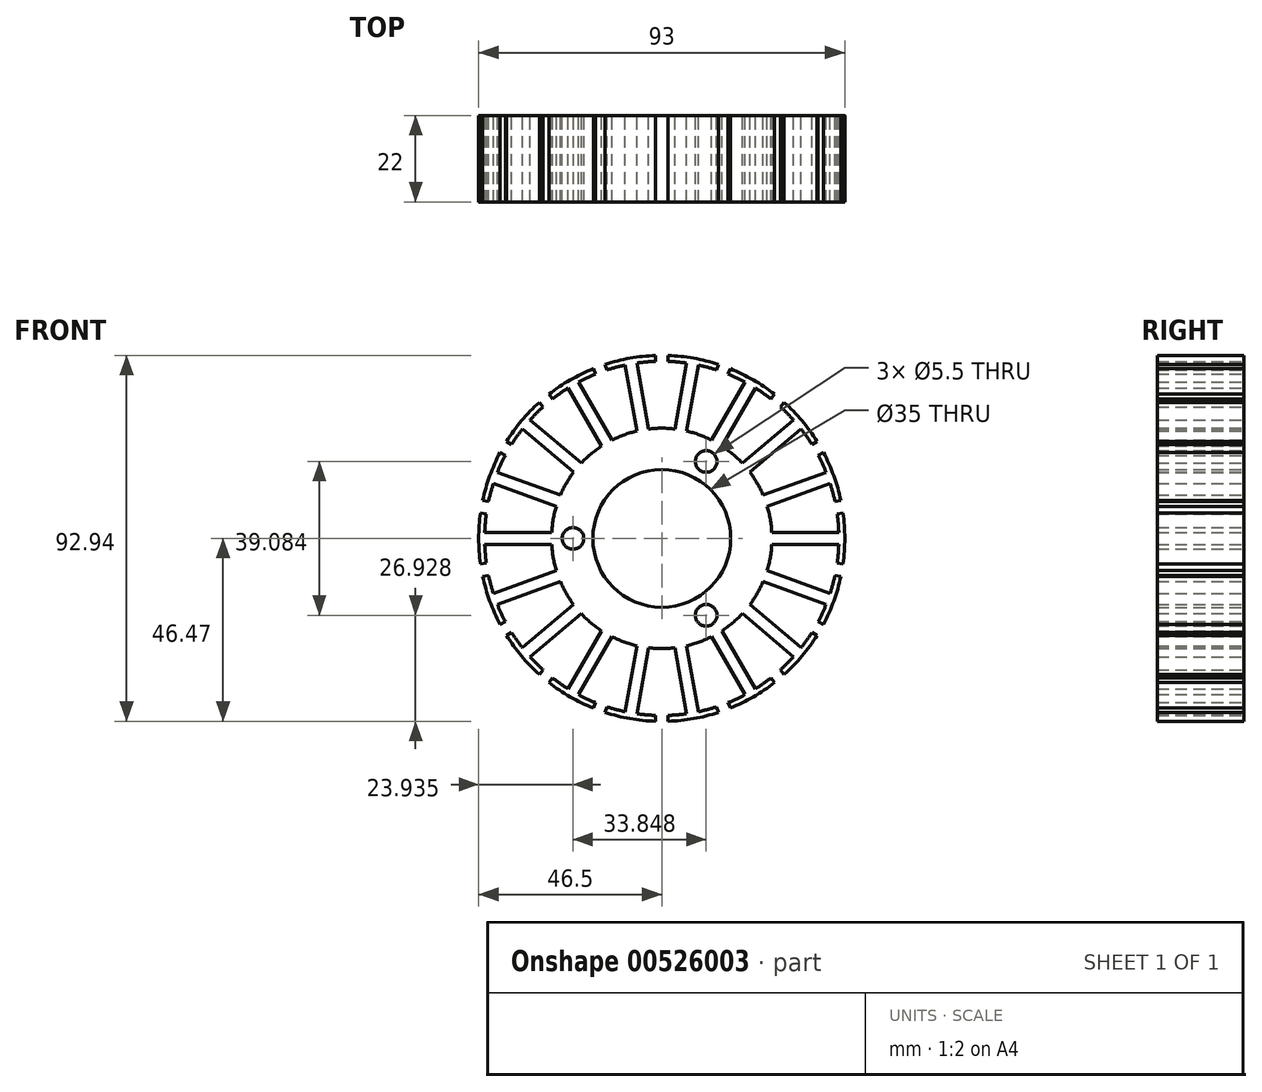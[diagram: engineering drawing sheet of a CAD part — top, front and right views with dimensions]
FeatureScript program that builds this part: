
annotation { "Feature Type Name" : "Feature", "Feature Type Description" : "" }
export const myFeature = defineFeature(function(context is Context, id is Id, definition is map)
    precondition{}
    {
        {
            var Q0;
            Q0=qCreatedBy(makeId("Front.planeOp"),FACE);
            var sketch = newSketch(context, id + "F0", { "sketchPlane" : qUnion([Q0])});
            skCircle(sketch, "E0", {"center": v(0, 0) * mm, "radius": 17.5 * mm});
            skArc(sketch, "E1", {"start": v(-46.04, 6.5) * mm, "mid": v(-46.5, 0) * mm, "end": v(-46.04, -6.5) * mm});
            skArc(sketch, "E2", {"start": v(-27.96, -1.5) * mm, "mid": v(-27.57, -4.86) * mm, "end": v(-26.79, -8.15) * mm});
            skLineSegment(sketch, "E3", {"start": v(-27.96, 1.5) * mm, "end": v(-44.97, 1.5) * mm});
            skLineSegment(sketch, "E4", {"start": v(-27.96, -1.5) * mm, "end": v(-44.97, -1.5) * mm});
            skArc(sketch, "E5", {"start": v(-44.56, 6.25) * mm, "mid": v(-44.83, 3.88) * mm, "end": v(-44.97, 1.5) * mm});
            skLineSegment(sketch, "E6", {"start": v(-46.04, 6.5) * mm, "end": v(-44.56, 6.25) * mm});
            skLineSegment(sketch, "E7", {"start": v(-46.04, -6.5) * mm, "end": v(-44.56, -6.25) * mm});
            skArc(sketch, "E8.trimOffspring", {"start": v(-44.97, -1.5) * mm, "mid": v(-44.83, -3.88) * mm, "end": v(-44.56, -6.25) * mm});
            skLineSegment(sketch, "E9.1.0", {"start": v(-26.79, 8.15) * mm, "end": v(-42.78, 13.97) * mm});
            skArc(sketch, "E9.1.1", {"start": v(-39.74, 21.11) * mm, "mid": v(-40.8, 18.98) * mm, "end": v(-41.75, 16.8) * mm});
            skArc(sketch, "E9.1.2", {"start": v(-42.78, 13.97) * mm, "mid": v(-43.46, 11.69) * mm, "end": v(-44.01, 9.37) * mm});
            skLineSegment(sketch, "E9.1.3", {"start": v(-25.76, 10.97) * mm, "end": v(-41.75, 16.8) * mm});
            skArc(sketch, "E9.1.4", {"start": v(-41.04, 21.86) * mm, "mid": v(-43.7, 15.9) * mm, "end": v(-45.49, 9.64) * mm});
            skLineSegment(sketch, "E9.1.5", {"start": v(-41.04, 21.86) * mm, "end": v(-39.74, 21.11) * mm});
            skLineSegment(sketch, "E9.1.6", {"start": v(-45.49, 9.64) * mm, "end": v(-44.01, 9.37) * mm});
            skLineSegment(sketch, "E9.2.0", {"start": v(-22.38, 16.82) * mm, "end": v(-35.42, 27.76) * mm});
            skArc(sketch, "E9.2.1", {"start": v(-30.12, 33.43) * mm, "mid": v(-31.85, 31.8) * mm, "end": v(-33.49, 30.06) * mm});
            skArc(sketch, "E9.2.2", {"start": v(-35.42, 27.76) * mm, "mid": v(-36.84, 25.85) * mm, "end": v(-38.16, 23.86) * mm});
            skLineSegment(sketch, "E9.2.3", {"start": v(-20.45, 19.12) * mm, "end": v(-33.49, 30.06) * mm});
            skArc(sketch, "E9.2.4", {"start": v(-31.1, 34.58) * mm, "mid": v(-35.62, 29.89) * mm, "end": v(-39.45, 24.62) * mm});
            skLineSegment(sketch, "E9.2.5", {"start": v(-31.1, 34.58) * mm, "end": v(-30.12, 33.43) * mm});
            skLineSegment(sketch, "E9.2.6", {"start": v(-39.45, 24.62) * mm, "end": v(-38.16, 23.86) * mm});
            skLineSegment(sketch, "E9.3.0", {"start": v(-15.28, 23.46) * mm, "end": v(-23.79, 38.2) * mm});
            skArc(sketch, "E9.3.1", {"start": v(-16.87, 41.72) * mm, "mid": v(-19.06, 40.77) * mm, "end": v(-21.19, 39.7) * mm});
            skArc(sketch, "E9.3.2", {"start": v(-23.79, 38.2) * mm, "mid": v(-25.78, 36.89) * mm, "end": v(-27.7, 35.47) * mm});
            skLineSegment(sketch, "E9.3.3", {"start": v(-12.68, 24.96) * mm, "end": v(-21.19, 39.7) * mm});
            skArc(sketch, "E9.3.4", {"start": v(-17.4, 43.12) * mm, "mid": v(-23.25, 40.27) * mm, "end": v(-28.65, 36.62) * mm});
            skLineSegment(sketch, "E9.3.5", {"start": v(-17.4, 43.12) * mm, "end": v(-16.87, 41.72) * mm});
            skLineSegment(sketch, "E9.3.6", {"start": v(-28.65, 36.62) * mm, "end": v(-27.7, 35.47) * mm});
            skLineSegment(sketch, "E9.4.0", {"start": v(-6.33, 27.27) * mm, "end": v(-9.29, 44.03) * mm});
            skArc(sketch, "E9.4.1", {"start": v(-1.58, 44.97) * mm, "mid": v(-3.96, 44.83) * mm, "end": v(-6.33, 44.55) * mm});
            skArc(sketch, "E9.4.2", {"start": v(-9.29, 44.03) * mm, "mid": v(-11.6, 43.48) * mm, "end": v(-13.9, 42.8) * mm});
            skLineSegment(sketch, "E9.4.3", {"start": v(-3.38, 27.8) * mm, "end": v(-6.33, 44.55) * mm});
            skArc(sketch, "E9.4.4", {"start": v(-1.6, 46.47) * mm, "mid": v(-8.07, 45.8) * mm, "end": v(-14.4, 44.22) * mm});
            skLineSegment(sketch, "E9.4.5", {"start": v(-1.6, 46.47) * mm, "end": v(-1.58, 44.97) * mm});
            skLineSegment(sketch, "E9.4.6", {"start": v(-14.4, 44.22) * mm, "end": v(-13.9, 42.8) * mm});
            skLineSegment(sketch, "E9.5.0", {"start": v(3.38, 27.8) * mm, "end": v(6.33, 44.55) * mm});
            skArc(sketch, "E9.5.1", {"start": v(13.9, 42.8) * mm, "mid": v(11.6, 43.48) * mm, "end": v(9.29, 44.03) * mm});
            skArc(sketch, "E9.5.2", {"start": v(6.33, 44.55) * mm, "mid": v(3.96, 44.83) * mm, "end": v(1.58, 44.97) * mm});
            skLineSegment(sketch, "E9.5.3", {"start": v(6.33, 27.27) * mm, "end": v(9.29, 44.03) * mm});
            skArc(sketch, "E9.5.4", {"start": v(14.4, 44.22) * mm, "mid": v(8.07, 45.8) * mm, "end": v(1.6, 46.47) * mm});
            skLineSegment(sketch, "E9.5.5", {"start": v(14.4, 44.22) * mm, "end": v(13.9, 42.8) * mm});
            skLineSegment(sketch, "E9.5.6", {"start": v(1.6, 46.47) * mm, "end": v(1.58, 44.97) * mm});
            skLineSegment(sketch, "E9.6.0", {"start": v(12.68, 24.96) * mm, "end": v(21.19, 39.7) * mm});
            skArc(sketch, "E9.6.1", {"start": v(27.7, 35.47) * mm, "mid": v(25.78, 36.89) * mm, "end": v(23.79, 38.2) * mm});
            skArc(sketch, "E9.6.2", {"start": v(21.19, 39.7) * mm, "mid": v(19.06, 40.77) * mm, "end": v(16.87, 41.72) * mm});
            skLineSegment(sketch, "E9.6.3", {"start": v(15.28, 23.46) * mm, "end": v(23.79, 38.2) * mm});
            skArc(sketch, "E9.6.4", {"start": v(28.65, 36.62) * mm, "mid": v(23.25, 40.27) * mm, "end": v(17.4, 43.12) * mm});
            skLineSegment(sketch, "E9.6.5", {"start": v(28.65, 36.62) * mm, "end": v(27.7, 35.47) * mm});
            skLineSegment(sketch, "E9.6.6", {"start": v(17.4, 43.12) * mm, "end": v(16.87, 41.72) * mm});
            skLineSegment(sketch, "E9.7.0", {"start": v(20.45, 19.12) * mm, "end": v(33.49, 30.06) * mm});
            skArc(sketch, "E9.7.1", {"start": v(38.16, 23.86) * mm, "mid": v(36.84, 25.85) * mm, "end": v(35.42, 27.76) * mm});
            skArc(sketch, "E9.7.2", {"start": v(33.49, 30.06) * mm, "mid": v(31.85, 31.8) * mm, "end": v(30.12, 33.43) * mm});
            skLineSegment(sketch, "E9.7.3", {"start": v(22.38, 16.82) * mm, "end": v(35.42, 27.76) * mm});
            skArc(sketch, "E9.7.4", {"start": v(39.45, 24.62) * mm, "mid": v(35.62, 29.89) * mm, "end": v(31.1, 34.58) * mm});
            skLineSegment(sketch, "E9.7.5", {"start": v(39.45, 24.62) * mm, "end": v(38.16, 23.86) * mm});
            skLineSegment(sketch, "E9.7.6", {"start": v(31.1, 34.58) * mm, "end": v(30.12, 33.43) * mm});
            skLineSegment(sketch, "E9.8.0", {"start": v(25.76, 10.97) * mm, "end": v(41.75, 16.8) * mm});
            skArc(sketch, "E9.8.1", {"start": v(44.01, 9.37) * mm, "mid": v(43.46, 11.69) * mm, "end": v(42.78, 13.97) * mm});
            skArc(sketch, "E9.8.2", {"start": v(41.75, 16.8) * mm, "mid": v(40.8, 18.98) * mm, "end": v(39.74, 21.11) * mm});
            skLineSegment(sketch, "E9.8.3", {"start": v(26.79, 8.15) * mm, "end": v(42.78, 13.97) * mm});
            skArc(sketch, "E9.8.4", {"start": v(45.49, 9.64) * mm, "mid": v(43.7, 15.9) * mm, "end": v(41.04, 21.86) * mm});
            skLineSegment(sketch, "E9.8.5", {"start": v(45.49, 9.64) * mm, "end": v(44.01, 9.37) * mm});
            skLineSegment(sketch, "E9.8.6", {"start": v(41.04, 21.86) * mm, "end": v(39.74, 21.11) * mm});
            skLineSegment(sketch, "E9.9.0", {"start": v(27.96, 1.5) * mm, "end": v(44.97, 1.5) * mm});
            skArc(sketch, "E9.9.1", {"start": v(44.56, -6.25) * mm, "mid": v(44.83, -3.88) * mm, "end": v(44.97, -1.5) * mm});
            skArc(sketch, "E9.9.2", {"start": v(44.97, 1.5) * mm, "mid": v(44.83, 3.88) * mm, "end": v(44.56, 6.25) * mm});
            skLineSegment(sketch, "E9.9.3", {"start": v(27.96, -1.5) * mm, "end": v(44.97, -1.5) * mm});
            skArc(sketch, "E9.9.4", {"start": v(46.04, -6.5) * mm, "mid": v(46.5, 0) * mm, "end": v(46.04, 6.5) * mm});
            skLineSegment(sketch, "E9.9.5", {"start": v(46.04, -6.5) * mm, "end": v(44.56, -6.25) * mm});
            skLineSegment(sketch, "E9.9.6", {"start": v(46.04, 6.5) * mm, "end": v(44.56, 6.25) * mm});
            skLineSegment(sketch, "E9.10.0", {"start": v(26.79, -8.15) * mm, "end": v(42.78, -13.97) * mm});
            skArc(sketch, "E9.10.1", {"start": v(39.74, -21.11) * mm, "mid": v(40.8, -18.98) * mm, "end": v(41.75, -16.8) * mm});
            skArc(sketch, "E9.10.2", {"start": v(42.78, -13.97) * mm, "mid": v(43.46, -11.69) * mm, "end": v(44.01, -9.37) * mm});
            skLineSegment(sketch, "E9.10.3", {"start": v(25.76, -10.97) * mm, "end": v(41.75, -16.8) * mm});
            skArc(sketch, "E9.10.4", {"start": v(41.04, -21.86) * mm, "mid": v(43.7, -15.9) * mm, "end": v(45.49, -9.64) * mm});
            skLineSegment(sketch, "E9.10.5", {"start": v(41.04, -21.86) * mm, "end": v(39.74, -21.11) * mm});
            skLineSegment(sketch, "E9.10.6", {"start": v(45.49, -9.64) * mm, "end": v(44.01, -9.37) * mm});
            skLineSegment(sketch, "E9.11.0", {"start": v(22.38, -16.82) * mm, "end": v(35.42, -27.76) * mm});
            skArc(sketch, "E9.11.1", {"start": v(30.12, -33.43) * mm, "mid": v(31.85, -31.8) * mm, "end": v(33.49, -30.06) * mm});
            skArc(sketch, "E9.11.2", {"start": v(35.42, -27.76) * mm, "mid": v(36.84, -25.85) * mm, "end": v(38.16, -23.86) * mm});
            skLineSegment(sketch, "E9.11.3", {"start": v(20.45, -19.12) * mm, "end": v(33.49, -30.06) * mm});
            skArc(sketch, "E9.11.4", {"start": v(31.1, -34.58) * mm, "mid": v(35.62, -29.89) * mm, "end": v(39.45, -24.62) * mm});
            skLineSegment(sketch, "E9.11.5", {"start": v(31.1, -34.58) * mm, "end": v(30.12, -33.43) * mm});
            skLineSegment(sketch, "E9.11.6", {"start": v(39.45, -24.62) * mm, "end": v(38.16, -23.86) * mm});
            skLineSegment(sketch, "E9.12.0", {"start": v(15.28, -23.46) * mm, "end": v(23.79, -38.2) * mm});
            skArc(sketch, "E9.12.1", {"start": v(16.87, -41.72) * mm, "mid": v(19.06, -40.77) * mm, "end": v(21.19, -39.7) * mm});
            skArc(sketch, "E9.12.2", {"start": v(23.79, -38.2) * mm, "mid": v(25.78, -36.89) * mm, "end": v(27.7, -35.47) * mm});
            skLineSegment(sketch, "E9.12.3", {"start": v(12.68, -24.96) * mm, "end": v(21.19, -39.7) * mm});
            skArc(sketch, "E9.12.4", {"start": v(17.4, -43.12) * mm, "mid": v(23.25, -40.27) * mm, "end": v(28.65, -36.62) * mm});
            skLineSegment(sketch, "E9.12.5", {"start": v(17.4, -43.12) * mm, "end": v(16.87, -41.72) * mm});
            skLineSegment(sketch, "E9.12.6", {"start": v(28.65, -36.62) * mm, "end": v(27.7, -35.47) * mm});
            skLineSegment(sketch, "E9.13.0", {"start": v(6.33, -27.27) * mm, "end": v(9.29, -44.03) * mm});
            skArc(sketch, "E9.13.1", {"start": v(1.58, -44.97) * mm, "mid": v(3.96, -44.83) * mm, "end": v(6.33, -44.55) * mm});
            skArc(sketch, "E9.13.2", {"start": v(9.29, -44.03) * mm, "mid": v(11.6, -43.48) * mm, "end": v(13.9, -42.8) * mm});
            skLineSegment(sketch, "E9.13.3", {"start": v(3.38, -27.8) * mm, "end": v(6.33, -44.55) * mm});
            skArc(sketch, "E9.13.4", {"start": v(1.6, -46.47) * mm, "mid": v(8.07, -45.8) * mm, "end": v(14.4, -44.22) * mm});
            skLineSegment(sketch, "E9.13.5", {"start": v(1.6, -46.47) * mm, "end": v(1.58, -44.97) * mm});
            skLineSegment(sketch, "E9.13.6", {"start": v(14.4, -44.22) * mm, "end": v(13.9, -42.8) * mm});
            skLineSegment(sketch, "E9.14.0", {"start": v(-3.38, -27.8) * mm, "end": v(-6.33, -44.55) * mm});
            skArc(sketch, "E9.14.1", {"start": v(-13.9, -42.8) * mm, "mid": v(-11.6, -43.48) * mm, "end": v(-9.29, -44.03) * mm});
            skArc(sketch, "E9.14.2", {"start": v(-6.33, -44.55) * mm, "mid": v(-3.96, -44.83) * mm, "end": v(-1.58, -44.97) * mm});
            skLineSegment(sketch, "E9.14.3", {"start": v(-6.33, -27.27) * mm, "end": v(-9.29, -44.03) * mm});
            skArc(sketch, "E9.14.4", {"start": v(-14.4, -44.22) * mm, "mid": v(-8.07, -45.8) * mm, "end": v(-1.6, -46.47) * mm});
            skLineSegment(sketch, "E9.14.5", {"start": v(-14.4, -44.22) * mm, "end": v(-13.9, -42.8) * mm});
            skLineSegment(sketch, "E9.14.6", {"start": v(-1.6, -46.47) * mm, "end": v(-1.58, -44.97) * mm});
            skLineSegment(sketch, "E9.15.0", {"start": v(-12.68, -24.96) * mm, "end": v(-21.19, -39.7) * mm});
            skArc(sketch, "E9.15.1", {"start": v(-27.7, -35.47) * mm, "mid": v(-25.78, -36.89) * mm, "end": v(-23.79, -38.2) * mm});
            skArc(sketch, "E9.15.2", {"start": v(-21.19, -39.7) * mm, "mid": v(-19.06, -40.77) * mm, "end": v(-16.87, -41.72) * mm});
            skLineSegment(sketch, "E9.15.3", {"start": v(-15.28, -23.46) * mm, "end": v(-23.79, -38.2) * mm});
            skArc(sketch, "E9.15.4", {"start": v(-28.65, -36.62) * mm, "mid": v(-23.25, -40.27) * mm, "end": v(-17.4, -43.12) * mm});
            skLineSegment(sketch, "E9.15.5", {"start": v(-28.65, -36.62) * mm, "end": v(-27.7, -35.47) * mm});
            skLineSegment(sketch, "E9.15.6", {"start": v(-17.4, -43.12) * mm, "end": v(-16.87, -41.72) * mm});
            skLineSegment(sketch, "E9.16.0", {"start": v(-20.45, -19.12) * mm, "end": v(-33.49, -30.06) * mm});
            skArc(sketch, "E9.16.1", {"start": v(-38.16, -23.86) * mm, "mid": v(-36.84, -25.85) * mm, "end": v(-35.42, -27.76) * mm});
            skArc(sketch, "E9.16.2", {"start": v(-33.49, -30.06) * mm, "mid": v(-31.85, -31.8) * mm, "end": v(-30.12, -33.43) * mm});
            skLineSegment(sketch, "E9.16.3", {"start": v(-22.38, -16.82) * mm, "end": v(-35.42, -27.76) * mm});
            skArc(sketch, "E9.16.4", {"start": v(-39.45, -24.62) * mm, "mid": v(-35.62, -29.89) * mm, "end": v(-31.1, -34.58) * mm});
            skLineSegment(sketch, "E9.16.5", {"start": v(-39.45, -24.62) * mm, "end": v(-38.16, -23.86) * mm});
            skLineSegment(sketch, "E9.16.6", {"start": v(-31.1, -34.58) * mm, "end": v(-30.12, -33.43) * mm});
            skLineSegment(sketch, "E9.17.0", {"start": v(-25.76, -10.97) * mm, "end": v(-41.75, -16.8) * mm});
            skArc(sketch, "E9.17.1", {"start": v(-44.01, -9.37) * mm, "mid": v(-43.46, -11.69) * mm, "end": v(-42.78, -13.97) * mm});
            skArc(sketch, "E9.17.2", {"start": v(-41.75, -16.8) * mm, "mid": v(-40.8, -18.98) * mm, "end": v(-39.74, -21.11) * mm});
            skLineSegment(sketch, "E9.17.3", {"start": v(-26.79, -8.15) * mm, "end": v(-42.78, -13.97) * mm});
            skArc(sketch, "E9.17.4", {"start": v(-45.49, -9.64) * mm, "mid": v(-43.7, -15.9) * mm, "end": v(-41.04, -21.86) * mm});
            skLineSegment(sketch, "E9.17.5", {"start": v(-45.49, -9.64) * mm, "end": v(-44.01, -9.37) * mm});
            skLineSegment(sketch, "E9.17.6", {"start": v(-41.04, -21.86) * mm, "end": v(-39.74, -21.11) * mm});
            skLineSegment(sketch, "E9.anchor1", {"start": v(0, 0) * mm, "end": v(-46.04, 6.5) * mm, "construction": true});
            skLineSegment(sketch, "E9.anchor2", {"start": v(0, 0) * mm, "end": v(-45.49, -9.64) * mm, "construction": true});
            skArc(sketch, "E10.trimOffspring", {"start": v(-25.76, -10.97) * mm, "mid": v(-24.25, -14) * mm, "end": v(-22.38, -16.82) * mm});
            skArc(sketch, "E11.trimOffspring", {"start": v(-20.45, -19.12) * mm, "mid": v(-18, -21.45) * mm, "end": v(-15.28, -23.46) * mm});
            skArc(sketch, "E12.trimOffspring", {"start": v(-12.68, -24.96) * mm, "mid": v(-9.58, -26.31) * mm, "end": v(-6.33, -27.27) * mm});
            skArc(sketch, "E13.trimOffspring", {"start": v(-3.38, -27.8) * mm, "mid": v(0, -28) * mm, "end": v(3.38, -27.8) * mm});
            skArc(sketch, "E14.trimOffspring", {"start": v(6.33, -27.27) * mm, "mid": v(9.58, -26.31) * mm, "end": v(12.68, -24.96) * mm});
            skArc(sketch, "E15.trimOffspring", {"start": v(15.28, -23.46) * mm, "mid": v(18, -21.45) * mm, "end": v(20.45, -19.12) * mm});
            skArc(sketch, "E16.trimOffspring", {"start": v(22.38, -16.82) * mm, "mid": v(24.25, -14) * mm, "end": v(25.76, -10.97) * mm});
            skArc(sketch, "E17.trimOffspring", {"start": v(26.79, -8.15) * mm, "mid": v(27.57, -4.86) * mm, "end": v(27.96, -1.5) * mm});
            skArc(sketch, "E18.trimOffspring", {"start": v(27.96, 1.5) * mm, "mid": v(27.57, 4.86) * mm, "end": v(26.79, 8.15) * mm});
            skArc(sketch, "E19.trimOffspring", {"start": v(25.76, 10.97) * mm, "mid": v(24.25, 14) * mm, "end": v(22.38, 16.82) * mm});
            skArc(sketch, "E20.trimOffspring", {"start": v(20.45, 19.12) * mm, "mid": v(18, 21.45) * mm, "end": v(15.28, 23.46) * mm});
            skArc(sketch, "E21.trimOffspring", {"start": v(12.68, 24.96) * mm, "mid": v(9.58, 26.31) * mm, "end": v(6.33, 27.27) * mm});
            skArc(sketch, "E22.trimOffspring", {"start": v(3.38, 27.8) * mm, "mid": v(0, 28) * mm, "end": v(-3.38, 27.8) * mm});
            skArc(sketch, "E23.trimOffspring", {"start": v(-6.33, 27.27) * mm, "mid": v(-9.58, 26.31) * mm, "end": v(-12.68, 24.96) * mm});
            skArc(sketch, "E24.trimOffspring", {"start": v(-15.28, 23.46) * mm, "mid": v(-18, 21.45) * mm, "end": v(-20.45, 19.12) * mm});
            skArc(sketch, "E25.trimOffspring", {"start": v(-22.38, 16.82) * mm, "mid": v(-24.25, 14) * mm, "end": v(-25.76, 10.97) * mm});
            skArc(sketch, "E26.trimOffspring", {"start": v(-26.79, 8.15) * mm, "mid": v(-27.57, 4.86) * mm, "end": v(-27.96, 1.5) * mm});
            skCircle(sketch, "E27", {"center": v(-22.57, 0) * mm, "radius": 2.75 * mm});
            skCircle(sketch, "E28.1.0", {"center": v(11.28, -19.54) * mm, "radius": 2.75 * mm});
            skCircle(sketch, "E28.2.0", {"center": v(11.28, 19.54) * mm, "radius": 2.75 * mm});
            skSolve(sketch);
        }
        {
            var Q0;
            Q0=qSketchRegion(id+"F0",true);
            extrude(context, id + "F1", {"entities" : qUnion([Q0]), "endBound" : BoundingType.SYMMETRIC, "depth" : 22 * mm});
        }
    });
